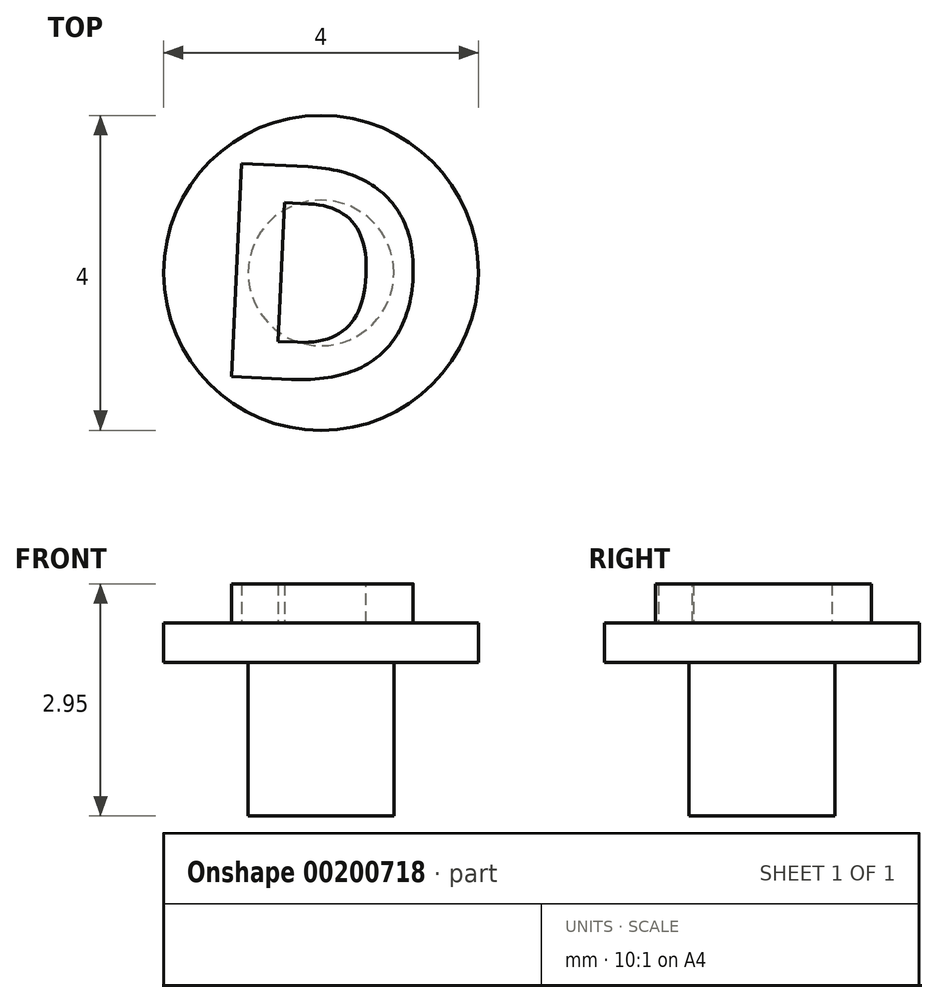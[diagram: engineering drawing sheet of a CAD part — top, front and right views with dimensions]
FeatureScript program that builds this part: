
annotation { "Feature Type Name" : "Feature", "Feature Type Description" : "" }
export const myFeature = defineFeature(function(context is Context, id is Id, definition is map)
    precondition{}
    {
        {
            var Q0;
            Q0=qCreatedBy(makeId("Top.planeOp"),FACE);
            var sketch = newSketch(context, id + "F0", { "sketchPlane" : qUnion([Q0])});
            skCircle(sketch, "E0", {"center": v(0, 0) * mm, "radius": 0.93 * mm});
            skSolve(sketch);
        }
        {
            var Q0;
            Q0 = qSketchRegion(id + "F0", true);
            extrude(context, id + "F1", {"entities" : qUnion([Q0]), "depth" : 1.95 * mm});
        }
        {
            var Q0;
            Q0=makeQuery(id+"F1.opExtrude","CAP_FACE",FACE,{"disambiguationData":[OSD([sQuery(id+"F0.wireOp",EDGE,"E0")])],"isStart":false});
            var sketch = newSketch(context, id + "F2", { "sketchPlane" : qUnion([Q0])});
            skPoint(sketch, "E1.0", {"position": v(0, 0) * mm});
            skCircle(sketch, "E2", {"center": v(0, 0) * mm, "radius": 2 * mm});
            skSolve(sketch);
        }
        {
            var Q0;
            Q0 = qSketchRegion(id + "F2", true);
            extrude(context, id + "F3", {"entities" : qUnion([Q0]), "operationType" : NewBodyOperationType.ADD, "depth" : 0.5 * mm});
        }
        {
            var Q0;
            Q0=makeQuery(id+"F3.opExtrude","CAP_FACE",FACE,{"disambiguationData":[OSD([sQuery(id+"F2.wireOp",EDGE,"E2")])],"isStart":false});
            var sketch = newSketch(context, id + "F4", { "sketchPlane" : qUnion([Q0])});
            skText(sketch, "E3", { "text": "D", "fontName": "OpenSans-Bold.ttf"});
            skPoint(sketch, "E4.0", {"position": v(0, 0) * mm});
            const initialGuessF4  = {"E3": [-0.00148, -0.0013, 0.9989, -0.04704, 0.00273]};
            skSetInitialGuess(sketch, initialGuessF4);
            skSolve(sketch);
        }
        {
            var Q0;
            Q0=makeQuery(id+"F4.imprint","IMPRINT",FACE,{"disambiguationData":[TD([[makeQuery(id+"F4.imprint","IMPRINT",EDGE,{"derivedFrom":sQuery(id+"F4.wireOp",EDGE,"E3.sketch_text.stroke-0")}),-1.0]])]});
            extrude(context, id + "F5", {"entities" : qUnion([Q0]), "operationType" : NewBodyOperationType.ADD, "depth" : 0.5 * mm});
        }
    });
